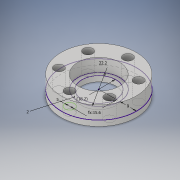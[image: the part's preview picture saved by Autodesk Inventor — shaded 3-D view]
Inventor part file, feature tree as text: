
AUTODESK INVENTOR PART (.ipt)
format: ipt  version: 2019 (Build 230136000, 136)  size: 136,704 bytes
history: native  units: in
note: dims shown in document units (in); Inventor stores cm internally (conversion verified against a paired STEP export)
features: extrude x3, sketch x1, pattern_circular x1
ambient origin geometry x8: Origin, YZ Plane, XZ Plane, XY Plane, X Axis, Y Axis, Z Axis, Center Point
bodies: Solid1 (feature_tree)
feature tree (5):
  sketch  "Sketch1"  dims[d0=0.874in d1=0.3543in d3=0.1969in d4=0.6142in d5=0.2756in d6=0.0in d9=0.0787in d10=0.1181in d11=0.0in d12=0.1181in d13=0.0in d14=2.3622in d15=360.0deg d17=0.7165in]
  extrude  "Extrusion1"  Depth=0.1181in
  extrude  "Extrusion3"  Depth=0.1181in
  extrude  "Extrusion4"  Depth=0.6142in
  pattern_circular  "Circular Pattern1"  [2 undecoded]
note: 2 required parameter values undecoded (feature->parameter linkage not recoverable at this tier; creation-order binding heuristic only, values carry confidence <= 0.55)
